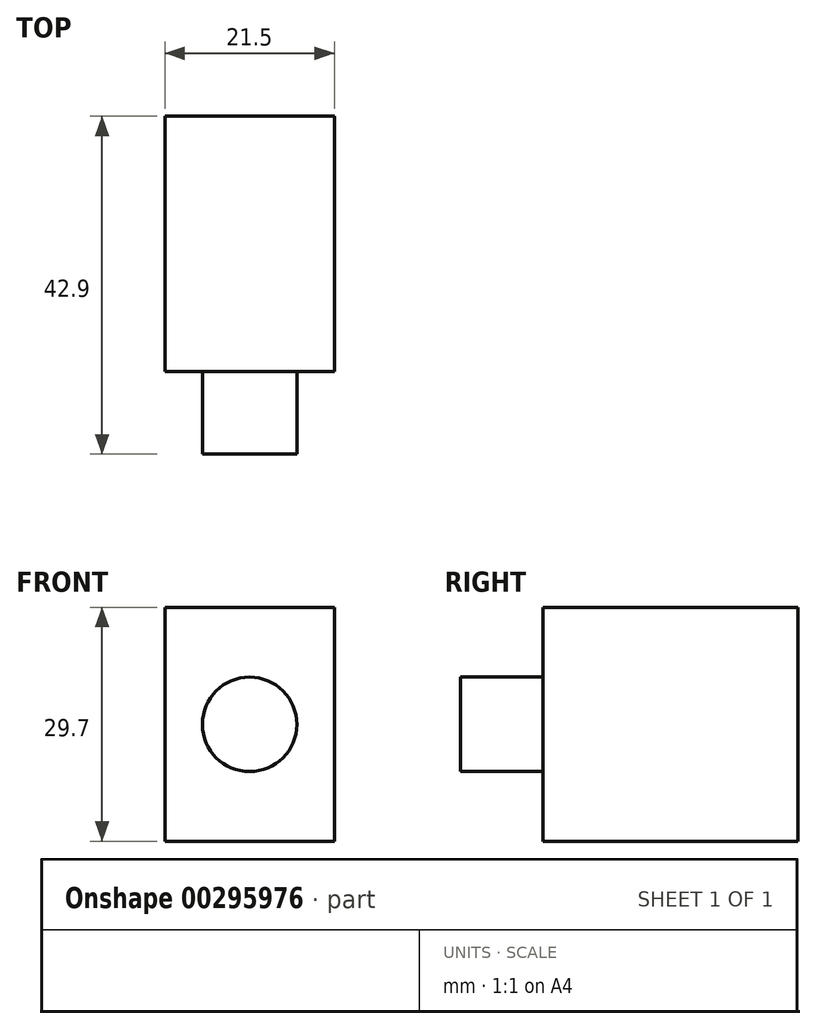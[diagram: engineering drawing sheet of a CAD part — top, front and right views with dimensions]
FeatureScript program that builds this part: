
annotation { "Feature Type Name" : "Feature", "Feature Type Description" : "" }
export const myFeature = defineFeature(function(context is Context, id is Id, definition is map)
    precondition{}
    {
        {
            var Q0;
            Q0=qCreatedBy(makeId("Front.planeOp"),FACE);
            var sketch = newSketch(context, id + "F0", { "sketchPlane" : qUnion([Q0])});
            skLineSegment(sketch, "E0.bottom", {"start": v(10.75, 14.85) * mm, "end": v(-10.75, 14.85) * mm});
            skLineSegment(sketch, "E0.top", {"start": v(10.75, -14.85) * mm, "end": v(-10.75, -14.85) * mm});
            skLineSegment(sketch, "E0.left", {"start": v(10.75, 14.85) * mm, "end": v(10.75, -14.85) * mm});
            skLineSegment(sketch, "E0.right", {"start": v(-10.75, 14.85) * mm, "end": v(-10.75, -14.85) * mm});
            skPoint(sketch, "E0.middle", {"position": v(0, 0) * mm});
            skSolve(sketch);
        }
        {
            var Q0;
            Q0=makeQuery(id+"F0.imprint","IMPRINT",FACE,{"disambiguationData":[TD([[makeQuery(id+"F0.imprint","IMPRINT",EDGE,{"derivedFrom":sQuery(id+"F0.wireOp",EDGE,"E0.bottom")}),1.0]])]});
            extrude(context, id + "F1", {"entities" : qUnion([Q0]), "oppositeDirection" : true, "depth" : 32.4 * mm, "offsetDistance" : 25 * mm});
        }
        {
            var Q0;
            Q0=makeQuery(id+"F1.opExtrude","CAP_FACE",FACE,{"disambiguationData":[OSD([sQuery(id+"F0.wireOp",EDGE,"E0.bottom"),sQuery(id+"F0.wireOp",EDGE,"E0.top"),sQuery(id+"F0.wireOp",EDGE,"E0.left"),sQuery(id+"F0.wireOp",EDGE,"E0.right")])],"isStart":true});
            var sketch = newSketch(context, id + "F2", { "sketchPlane" : qUnion([Q0])});
            skCircle(sketch, "E1", {"center": v(0, 0) * mm, "radius": 6 * mm});
            skSolve(sketch);
        }
        {
            var Q0;
            Q0=makeQuery(id+"F2.imprint","IMPRINT",FACE,{"disambiguationData":[TD([[makeQuery(id+"F2.imprint","IMPRINT",EDGE,{"derivedFrom":sQuery(id+"F2.wireOp",EDGE,"E1")}),1.0]])]});
            extrude(context, id + "F3", {"entities" : qUnion([Q0]), "operationType" : NewBodyOperationType.ADD, "depth" : 10.5 * mm, "offsetDistance" : 25 * mm});
        }
    });
